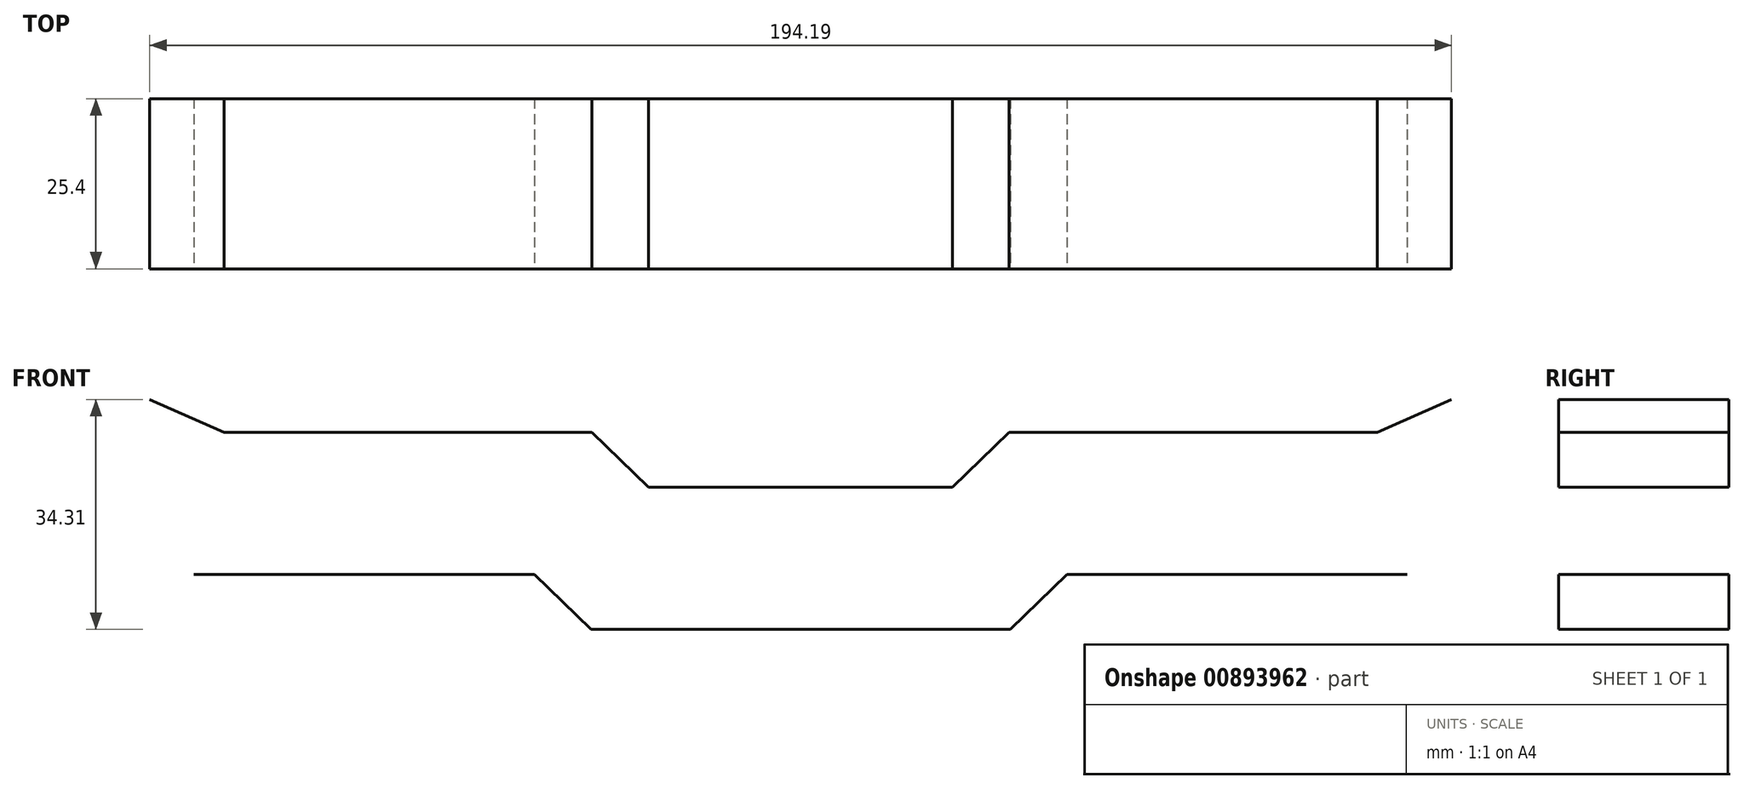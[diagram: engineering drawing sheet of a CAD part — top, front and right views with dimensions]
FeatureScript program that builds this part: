
annotation { "Feature Type Name" : "Feature", "Feature Type Description" : "" }
export const myFeature = defineFeature(function(context is Context, id is Id, definition is map)
    precondition{}
    {
        {
            var Q0;
            Q0=qCreatedBy(makeId("Front.planeOp"),FACE);
            var sketch = newSketch(context, id + "F0", { "sketchPlane" : qUnion([Q0])});
            skLineSegment(sketch, "E0", {"start": v(39.74, -11.2) * mm, "end": v(31.3, -19.37) * mm});
            skLineSegment(sketch, "E1", {"start": v(39.74, -11.2) * mm, "end": v(90.52, -11.2) * mm});
            skCircle(sketch, "E2", {"center": v(65.13, -11.2) * mm, "radius": 8.18 * mm});
            skLineSegment(sketch, "E3", {"start": v(90.52, -11.2) * mm, "end": v(121.99, 2.67) * mm});
            skLineSegment(sketch, "E4", {"start": v(121.99, 2.67) * mm, "end": v(121.99, 24.52) * mm});
            skLineSegment(sketch, "E5", {"start": v(121.99, 24.52) * mm, "end": v(-123.15, 24.52) * mm, "construction": true});
            skLineSegment(sketch, "E6.2", {"start": v(86.04, 10.06) * mm, "end": v(97.12, 14.94) * mm});
            skLineSegment(sketch, "E6.3", {"start": v(31.14, 10.06) * mm, "end": v(86.04, 10.06) * mm});
            skLineSegment(sketch, "E6.4", {"start": v(31.14, 10.06) * mm, "end": v(22.7, 1.88) * mm});
            skLineSegment(sketch, "E7", {"start": v(0.03, 49.43) * mm, "end": v(0.03, -29.25) * mm, "construction": true});
            skLineSegment(sketch, "E8", {"start": v(0.03, -19.37) * mm, "end": v(31.3, -19.37) * mm});
            skLineSegment(sketch, "E9", {"start": v(0.03, 1.88) * mm, "end": v(22.7, 1.88) * mm});
            skLineSegment(sketch, "E10.MirrorCS", {"start": v(0.03, -19.37) * mm, "end": v(-31.24, -19.37) * mm});
            skLineSegment(sketch, "E11.MirrorCS", {"start": v(0.03, 1.88) * mm, "end": v(-22.64, 1.88) * mm});
            skLineSegment(sketch, "E12.MirrorCS", {"start": v(-31.08, 10.06) * mm, "end": v(-22.64, 1.88) * mm});
            skLineSegment(sketch, "E13.MirrorCS", {"start": v(-39.69, -11.2) * mm, "end": v(-31.24, -19.37) * mm});
            skLineSegment(sketch, "E14.MirrorCS", {"start": v(-39.69, -11.2) * mm, "end": v(-90.46, -11.2) * mm});
            skLineSegment(sketch, "E15.MirrorCS", {"start": v(-31.08, 10.06) * mm, "end": v(-85.99, 10.06) * mm});
            skCircle(sketch, "E16.MirrorC", {"center": v(-65.08, -11.2) * mm, "radius": 8.18 * mm});
            skLineSegment(sketch, "E17.MirrorCS", {"start": v(-90.46, -11.2) * mm, "end": v(-121.93, 2.67) * mm});
            skLineSegment(sketch, "E18.MirrorCS", {"start": v(-85.99, 10.06) * mm, "end": v(-97.07, 14.94) * mm});
            skLineSegment(sketch, "E19.MirrorCS", {"start": v(-121.93, 2.67) * mm, "end": v(-121.93, 24.52) * mm});
            skSolve(sketch);
        }
        {
            var Q0;
            Q0 = qSketchRegion(id + "F0", true);
            var Q1;
            Q1=sQuery(id+"F0.wireOp",EDGE,"E15.MirrorCS");
            var Q2;
            Q2=sQuery(id+"F0.wireOp",EDGE,"E18.MirrorCS");
            var Q3;
            Q3=sQuery(id+"F0.wireOp",EDGE,"E14.MirrorCS");
            var Q4;
            Q4=sQuery(id+"F0.wireOp",EDGE,"E13.MirrorCS");
            var Q5;
            Q5=sQuery(id+"F0.wireOp",EDGE,"E12.MirrorCS");
            var Q6;
            Q6=sQuery(id+"F0.wireOp",EDGE,"E11.MirrorCS");
            var Q7;
            Q7=sQuery(id+"F0.wireOp",EDGE,"E10.MirrorCS");
            var Q8;
            Q8=sQuery(id+"F0.wireOp",EDGE,"E8");
            var Q9;
            Q9=sQuery(id+"F0.wireOp",EDGE,"E9");
            var Q10;
            Q10=sQuery(id+"F0.wireOp",EDGE,"E0");
            var Q11;
            Q11=sQuery(id+"F0.wireOp",EDGE,"E6.4");
            var Q12;
            Q12=sQuery(id+"F0.wireOp",EDGE,"E6.3");
            var Q13;
            Q13=sQuery(id+"F0.wireOp",EDGE,"E1");
            var Q14;
            Q14=sQuery(id+"F0.wireOp",EDGE,"E6.2");
            extrude(context, id + "F1", {"entities" : qUnion([Q0]), "bodyType" : ToolBodyType.SURFACE, "surfaceEntities" : qUnion([Q1, Q2, Q3, Q4, Q5, Q6, Q7, Q8, Q9, Q10, Q11, Q12, Q13, Q14]), "depth" : 25.4 * mm, "offsetDistance" : 25.4 * mm});
        }
    });
